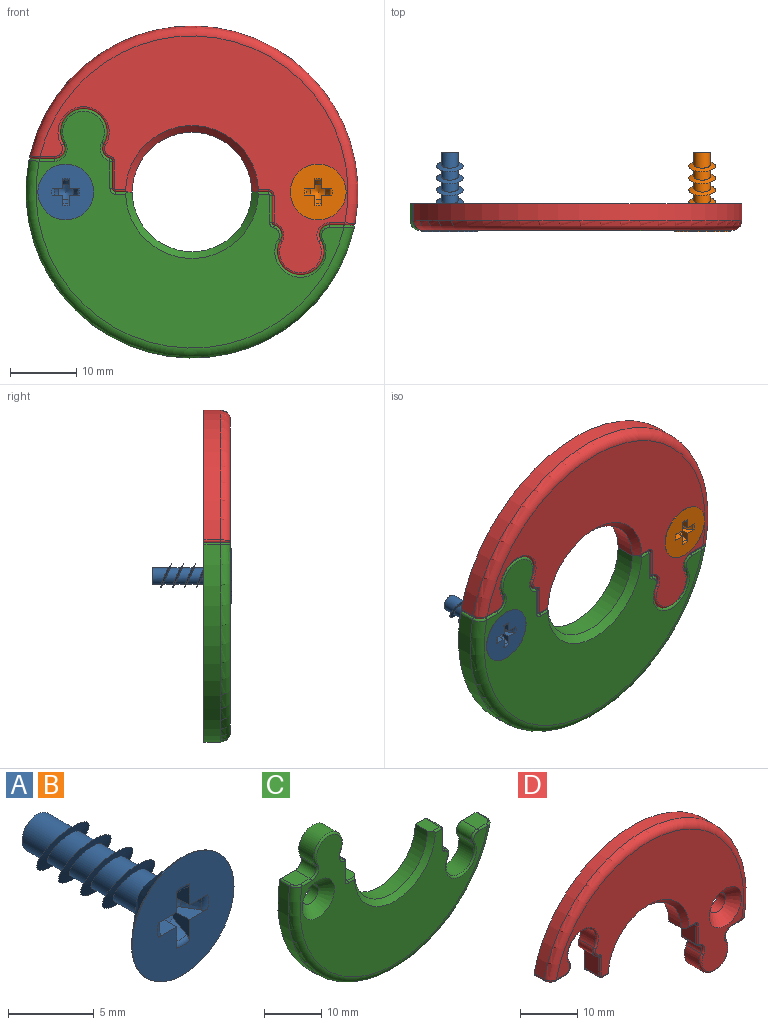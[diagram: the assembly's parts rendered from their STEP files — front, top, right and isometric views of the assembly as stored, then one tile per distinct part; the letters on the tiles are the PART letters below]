
ASSEMBLY  parts=4 mates=2
PART A: 34 faces, bbox 8.5x12.1x8.5 mm
  f0: plane 8.4x8.4mm, normal (0,-1,0), area 47.9mm2, adj f3,f18,f19,f20,f21,f26,f27,f28
  f1: cylinder r=1.25mm len=2.5mm, axis (0,-1,0), area 14.2mm2, adj f2,f5
  f2: cone r=1.25mm half-angle=49deg, axis (0,-1,0), area 66.9mm2, adj f1,f3
  f3: cylinder r=4.2mm len=8.4mm, axis (0,-1,0), area 0.9mm2, adj f0,f2
  f4: cone r=2mm half-angle=74deg, axis (0,-0.91,-0.41), area 7.3mm2, adj f5,f6
  f5: cone r=1.25mm half-angle=83deg, axis (0,0.91,0.41), area 7.7mm2, adj f1,f4
  f6: cylinder r=1.25mm len=2.6mm, axis (0,-1,0), area 12.2mm2, adj f4,f8
  f7: cone r=2mm half-angle=74deg, axis (0,-0.91,-0.41), area 7.3mm2, adj f8,f9
  f8: cone r=1.25mm half-angle=83deg, axis (0,0.91,0.41), area 7.7mm2, adj f6,f7
  f9: cylinder r=1.25mm len=2.6mm, axis (0,-1,0), area 12.2mm2, adj f7,f11
  f10: cone r=2mm half-angle=74deg, axis (0,-0.91,-0.41), area 7.3mm2, adj f11,f12
  f11: cone r=1.25mm half-angle=83deg, axis (0,0.91,0.41), area 7.7mm2, adj f9,f10
  f12: cylinder r=1.25mm len=2.6mm, axis (0,-1,0), area 12.2mm2, adj f10,f14
  f13: cone r=2mm half-angle=74deg, axis (0,-0.91,-0.41), area 7.5mm2, adj f14,f16
  f14: cone r=1.25mm half-angle=83deg, axis (0,0.91,0.41), area 7.7mm2, adj f12,f13
  f15: plane 2.5x2.5mm, normal (0,1,0), area 4.9mm2, adj f16
  f16: cylinder r=1.25mm len=2.5mm, axis (0,-1,0), area 14.8mm2, adj f13,f15
  f17: cone r=1.17mm half-angle=62deg, axis (0,-1,0), area 4.2mm2, adj f22,f23,f24,f25,f26,f27,f28,f29
  f18: torus R=2.1mm, axis (0,1,0), area 0.4mm2, adj f0,f22,f27,f32
  f19: torus R=2.1mm, axis (0,1,0), area 0.4mm2, adj f0,f23,f31,f33
  f20: torus R=2.1mm, axis (0,1,0), area 0.4mm2, adj f0,f24,f29,f30
  f21: torus R=2.1mm, axis (0,1,0), area 0.4mm2, adj f0,f25,f26,f28
  f22: cone r=1.17mm half-angle=28.4deg, axis (0,-1,0), area 1.4mm2, adj f17,f18,f27,f32
  f23: cone r=1.17mm half-angle=28.4deg, axis (0,-1,0), area 1.4mm2, adj f17,f19,f31,f33
  f24: cone r=1.17mm half-angle=28.4deg, axis (0,-1,0), area 1.4mm2, adj f17,f20,f29,f30
  f25: cone r=1.17mm half-angle=28.4deg, axis (0,-1,0), area 1.4mm2, adj f17,f21,f26,f28
  f26: plane 1.61x1.6mm, normal (1,0,0), area 1.3mm2, adj f0,f17,f21,f25,f27
  f27: plane 1.61x1.6mm, normal (0,0,1), area 1.3mm2, adj f0,f17,f18,f22,f26
  f28: plane 1.61x1.6mm, normal (-1,0,0), area 1.3mm2, adj f0,f17,f21,f25,f29
  f29: plane 1.61x1.6mm, normal (0,0,1), area 1.3mm2, adj f0,f17,f20,f24,f28
  f30: plane 1.61x1.6mm, normal (0,0,-1), area 1.3mm2, adj f0,f17,f20,f24,f31
  f31: plane 1.61x1.6mm, normal (-1,0,0), area 1.3mm2, adj f0,f17,f19,f23,f30
  f32: plane 1.61x1.6mm, normal (0,0,-1), area 1.3mm2, adj f0,f17,f18,f22,f33
  f33: plane 1.61x1.6mm, normal (1,0,0), area 1.3mm2, adj f0,f17,f19,f23,f32
PART B: same geometry as A
PART C: 44 faces, bbox 53.5x4x39.8 mm
  f0: plane 49.41x37.5mm, normal (0,1,0), area 841.9mm2, adj f4,f5,f6,f7,f8,f9,f10,f11
  f1: cone r=9mm half-angle=45deg, axis (0,-1,0), area 42.1mm2, adj f3,f4,f11,f23,f29,f41
  f2: torus R=23.5mm, axis (0,-1,0), area 179.3mm2, adj f3,f5,f15,f33
  f3: plane 46.38x35.65mm, normal (0,-1,0), area 639.2mm2, adj f1,f2,f16,f17,f18,f19,f20,f21
  f4: cylinder r=9mm len=18mm, axis (0,1,0), area 84.8mm2, adj f0,f1,f11,f29
  f5: cylinder r=25mm len=49.4mm, axis (0,1,0), area 194.5mm2, adj f0,f2,f14,f32
  f6: plane 3.65x3.4mm, normal (0,0,1), area 12.1mm2, adj f0,f7,f14,f15,f16
  f7: cylinder r=1.5mm len=3.65mm, axis (0,-1,0), area 11.5mm2, adj f0,f6,f8,f17
  f8: cylinder r=3.5mm len=7mm, axis (0,-1,0), area 53.5mm2, adj f0,f7,f9,f18
  f9: cylinder r=1.5mm len=3.65mm, axis (0,-1,0), area 10.1mm2, adj f0,f8,f12,f19
  f10: plane 4.06x3.65mm, normal (1,0,0), area 14.8mm2, adj f0,f12,f13,f21
  f11: plane 3.65x2.5mm, normal (0,0,1), area 8.9mm2, adj f0,f1,f4,f13,f23
  f12: cylinder r=0.5mm len=3.65mm, axis (0,-1,0), area 2.4mm2, adj f0,f9,f10,f20
  f13: cylinder r=0.5mm len=3.65mm, axis (0,-1,0), area 2.9mm2, adj f0,f10,f11,f22
  f14: cylinder r=0.35mm len=2.5mm, axis (0,1,0), area 1.6mm2, adj f0,f5,f6,f15
  f15: bspline ~1.96x1.59mm, area 1.3mm2, adj f2,f6,f14,f16
  f16: cylinder r=0.35mm len=2.22mm, axis (-1,0,0), area 1.2mm2, adj f3,f6,f15,f17
  f17: torus R=1.15mm, axis (0,-1,0), area 1.6mm2, adj f3,f7,f16,f18
  f18: torus R=3.85mm, axis (0,-1,0), area 8.4mm2, adj f3,f8,f17,f19
  f19: torus R=1.15mm, axis (0,-1,0), area 1.4mm2, adj f3,f9,f18,f20
  f20: torus R=0.85mm, axis (0,-1,0), area 0.5mm2, adj f3,f12,f19,f21
  f21: cylinder r=0.35mm len=4.06mm, axis (0,0,1), area 2.2mm2, adj f3,f10,f20,f22
  f22: torus R=0.15mm, axis (0,-1,0), area 0.3mm2, adj f3,f13,f21,f23
  f23: cylinder r=0.35mm len=1.85mm, axis (-1,0,0), area 0.9mm2, adj f1,f3,f11,f22
  f24: plane 3.65x3.55mm, normal (0,0,1), area 12.7mm2, adj f0,f25,f32,f33,f34
  f25: cylinder r=1.5mm len=3.65mm, axis (0,-1,0), area 11.5mm2, adj f0,f24,f26,f35
  f26: cylinder r=3.5mm len=7mm, axis (0,-1,0), area 53.5mm2, adj f0,f25,f27,f36
  f27: cylinder r=1.5mm len=3.65mm, axis (0,-1,0), area 10.1mm2, adj f0,f26,f30,f37
  f28: plane 4.06x3.65mm, normal (1,0,0), area 14.8mm2, adj f0,f30,f31,f39
  f29: plane 3.65x2.5mm, normal (0,0,1), area 8.9mm2, adj f0,f1,f4,f31,f41
  f30: cylinder r=0.5mm len=3.65mm, axis (0,-1,0), area 2.4mm2, adj f0,f27,f28,f38
  f31: cylinder r=0.5mm len=3.65mm, axis (0,-1,0), area 2.9mm2, adj f0,f28,f29,f40
  f32: cylinder r=0.35mm len=2.5mm, axis (0,1,0), area 1.2mm2, adj f0,f5,f24,f33
  f33: bspline ~1.86x1.59mm, area 1.1mm2, adj f2,f24,f32,f34
  f34: cylinder r=0.35mm len=2.38mm, axis (-1,0,0), area 1.3mm2, adj f3,f24,f33,f35
  f35: torus R=1.85mm, axis (0,-1,0), area 1.9mm2, adj f3,f25,f34,f36
  f36: torus R=3.15mm, axis (0,-1,0), area 7.8mm2, adj f3,f26,f35,f37
  f37: torus R=1.85mm, axis (0,-1,0), area 1.6mm2, adj f3,f27,f36,f38
  f38: torus R=0.15mm, axis (0,-1,0), area 0.3mm2, adj f3,f30,f37,f39
  f39: cylinder r=0.35mm len=4.06mm, axis (0,0,1), area 2.2mm2, adj f3,f28,f38,f40
  f40: torus R=0.85mm, axis (0,-1,0), area 0.5mm2, adj f3,f31,f39,f41
  f41: cylinder r=0.35mm len=1.85mm, axis (-1,0,0), area 0.9mm2, adj f1,f3,f29,f40
  f42: cylinder r=2mm len=4mm, axis (0,-1,0), area 25.1mm2, adj f0,f43
  f43: cone r=2mm half-angle=45deg, axis (0,-1,0), area 53.3mm2, adj f3,f42
PART D: 44 faces, bbox 53.5x4x39.8 mm
  f0: plane 49.41x37.5mm, normal (0,1,0), area 841.9mm2, adj f4,f5,f6,f7,f8,f9,f10,f11
  f1: cone r=9mm half-angle=45deg, axis (0,-1,0), area 42.1mm2, adj f3,f4,f11,f23,f29,f41
  f2: torus R=23.5mm, axis (0,-1,0), area 179.3mm2, adj f3,f5,f15,f33
  f3: plane 46.38x35.65mm, normal (0,-1,0), area 639.2mm2, adj f1,f2,f16,f17,f18,f19,f20,f21
  f4: cylinder r=9mm len=18mm, axis (0,1,0), area 84.8mm2, adj f0,f1,f11,f29
  f5: cylinder r=25mm len=49.4mm, axis (0,1,0), area 194.5mm2, adj f0,f2,f14,f32
  f6: plane 3.65x3.4mm, normal (0,0,-1), area 12.1mm2, adj f0,f7,f14,f15,f16
  f7: cylinder r=1.5mm len=3.65mm, axis (0,-1,0), area 11.5mm2, adj f0,f6,f8,f17
  f8: cylinder r=3.5mm len=7mm, axis (0,-1,0), area 53.5mm2, adj f0,f7,f9,f18
  f9: cylinder r=1.5mm len=3.65mm, axis (0,-1,0), area 10.1mm2, adj f0,f8,f12,f19
  f10: plane 4.06x3.65mm, normal (-1,0,0), area 14.8mm2, adj f0,f12,f13,f21
  f11: plane 3.65x2.5mm, normal (0,0,-1), area 8.9mm2, adj f0,f1,f4,f13,f23
  f12: cylinder r=0.5mm len=3.65mm, axis (0,-1,0), area 2.4mm2, adj f0,f9,f10,f20
  f13: cylinder r=0.5mm len=3.65mm, axis (0,-1,0), area 2.9mm2, adj f0,f10,f11,f22
  f14: cylinder r=0.35mm len=2.5mm, axis (0,1,0), area 1.6mm2, adj f0,f5,f6,f15
  f15: bspline ~1.96x1.59mm, area 1.3mm2, adj f2,f6,f14,f16
  f16: cylinder r=0.35mm len=2.22mm, axis (1,0,0), area 1.2mm2, adj f3,f6,f15,f17
  f17: torus R=1.15mm, axis (0,-1,0), area 1.6mm2, adj f3,f7,f16,f18
  f18: torus R=3.85mm, axis (0,-1,0), area 8.4mm2, adj f3,f8,f17,f19
  f19: torus R=1.15mm, axis (0,-1,0), area 1.4mm2, adj f3,f9,f18,f20
  f20: torus R=0.85mm, axis (0,-1,0), area 0.5mm2, adj f3,f12,f19,f21
  f21: cylinder r=0.35mm len=4.06mm, axis (0,0,-1), area 2.2mm2, adj f3,f10,f20,f22
  f22: torus R=0.15mm, axis (0,-1,0), area 0.3mm2, adj f3,f13,f21,f23
  f23: cylinder r=0.35mm len=1.85mm, axis (1,0,0), area 0.9mm2, adj f1,f3,f11,f22
  f24: plane 3.65x3.55mm, normal (0,0,-1), area 12.7mm2, adj f0,f25,f32,f33,f34
  f25: cylinder r=1.5mm len=3.65mm, axis (0,-1,0), area 11.5mm2, adj f0,f24,f26,f35
  f26: cylinder r=3.5mm len=7mm, axis (0,-1,0), area 53.5mm2, adj f0,f25,f27,f36
  f27: cylinder r=1.5mm len=3.65mm, axis (0,-1,0), area 10.1mm2, adj f0,f26,f30,f37
  f28: plane 4.06x3.65mm, normal (-1,0,0), area 14.8mm2, adj f0,f30,f31,f39
  f29: plane 3.65x2.5mm, normal (0,0,-1), area 8.9mm2, adj f0,f1,f4,f31,f41
  f30: cylinder r=0.5mm len=3.65mm, axis (0,-1,0), area 2.4mm2, adj f0,f27,f28,f38
  f31: cylinder r=0.5mm len=3.65mm, axis (0,-1,0), area 2.9mm2, adj f0,f28,f29,f40
  f32: cylinder r=0.35mm len=2.5mm, axis (0,1,0), area 1.2mm2, adj f0,f5,f24,f33
  f33: bspline ~1.86x1.59mm, area 1.1mm2, adj f2,f24,f32,f34
  f34: cylinder r=0.35mm len=2.38mm, axis (1,0,0), area 1.3mm2, adj f3,f24,f33,f35
  f35: torus R=1.85mm, axis (0,-1,0), area 1.9mm2, adj f3,f25,f34,f36
  f36: torus R=3.15mm, axis (0,-1,0), area 7.8mm2, adj f3,f26,f35,f37
  f37: torus R=1.85mm, axis (0,-1,0), area 1.6mm2, adj f3,f27,f36,f38
  f38: torus R=0.15mm, axis (0,-1,0), area 0.3mm2, adj f3,f30,f37,f39
  f39: cylinder r=0.35mm len=4.06mm, axis (0,0,-1), area 2.2mm2, adj f3,f28,f38,f40
  f40: torus R=0.85mm, axis (0,-1,0), area 0.5mm2, adj f3,f31,f39,f41
  f41: cylinder r=0.35mm len=1.85mm, axis (1,0,0), area 0.9mm2, adj f1,f3,f29,f40
  f42: cylinder r=2mm len=4mm, axis (0,-1,0), area 25.1mm2, adj f0,f43
  f43: cone r=2mm half-angle=45deg, axis (0,-1,0), area 53.3mm2, adj f3,f42
PLACE A t=(-19,-1.61,0)mm
PLACE B t=(19,-1.61,0)mm
PLACE C at identity
PLACE D at identity fixed
MATE fastened B.f2 <-> D.f42  axis (0,1,0) through (19,-4,0)mm
MATE fastened A.f2 <-> C.f43  axis (0,1,0) through (-19,-4,0)mm
